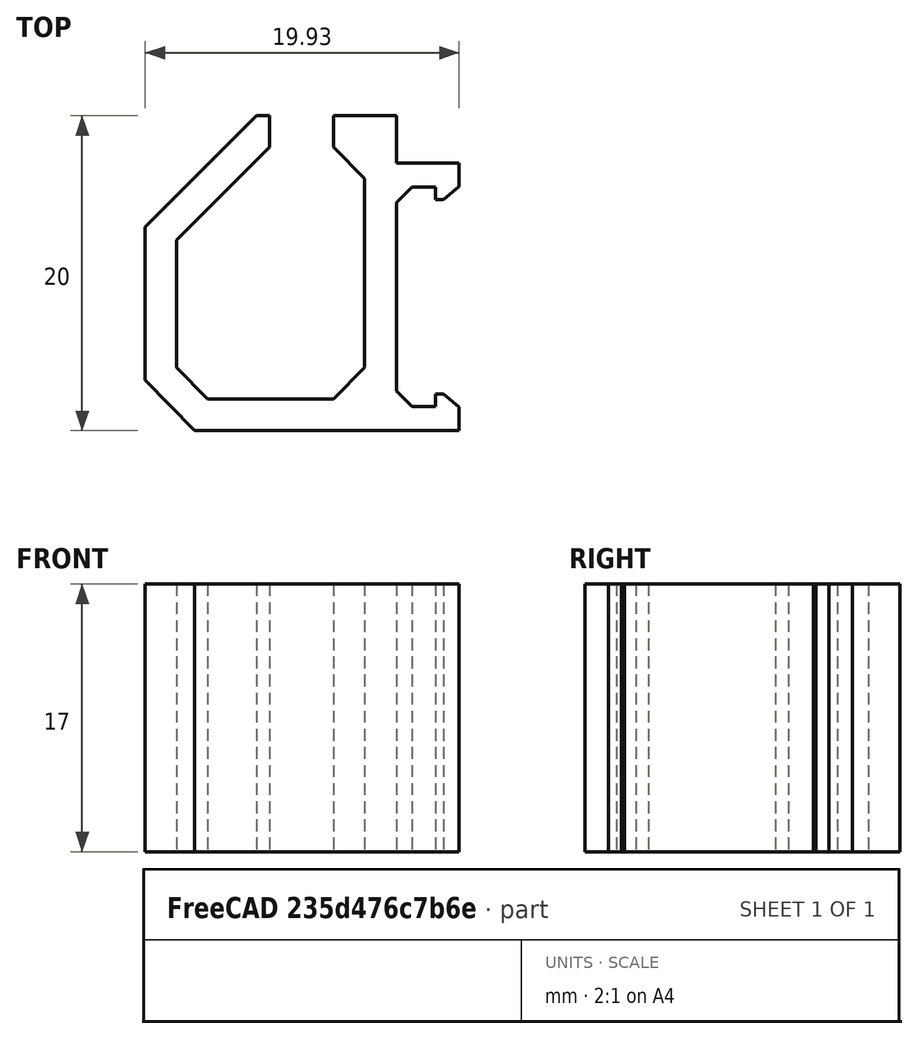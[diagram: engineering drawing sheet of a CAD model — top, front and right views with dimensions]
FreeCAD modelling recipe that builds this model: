
FCSTD DOCUMENT  (FreeCAD 1.1R)
Label: Clip
License: All rights reserved
LicenseURL: https://en.wikipedia.org/wiki/All_rights_reserved
objects: App::Point×1, Sketcher::SketchObject×1, PartDesign::Pad×1, PartDesign::Body×1
note: 6 computed .brp shape members not serialized (recipe doc carries the construction recipe); baked Part::Feature solids carry a one-line shape summary decoded from their .brp

FEATURE [App::Point] Origin001
  Role = Origin
FEATURE [Sketcher::SketchObject] Sketch
  ArcFitTolerance = 1e-06
  AttachmentSupport = -> [Origin]
  ExternalTypes = [0]
  FullyConstrained = false
  MakeInternals = false
  MapMode = 5
  sketch-geometry (38):
    g0: LineSegment StartX=6 StartY=1.52 StartZ=0 EndX=6 EndY=2.32 EndZ=0
    g1: LineSegment StartX=6 StartY=2.32 StartZ=0 EndX=6.5 EndY=2.32 EndZ=0
    g2: LineSegment StartX=6.5 StartY=2.32 StartZ=0 EndX=7.5 EndY=1.5 EndZ=0
    g3: LineSegment StartX=7.5 StartY=1.5 StartZ=0 EndX=7.5 EndY=0 EndZ=0
    g4: LineSegment StartX=7.5 StartY=0 StartZ=0 EndX=-9.3 EndY=0 EndZ=0
    g5: LineSegment StartX=6 StartY=14.68 StartZ=0 EndX=6.5 EndY=14.68 EndZ=0
    g6: LineSegment StartX=6.5 StartY=14.68 StartZ=0 EndX=7.5 EndY=15.5 EndZ=0
    g7: LineSegment StartX=7.5 StartY=15.5 StartZ=0 EndX=7.5 EndY=17 EndZ=0
    g8: LineSegment StartX=7.5 StartY=17 StartZ=0 EndX=3.52 EndY=17 EndZ=0
    g9: LineSegment StartX=6 StartY=14.68 StartZ=0 EndX=6 EndY=15.48 EndZ=0
    g10: LineSegment StartX=6 StartY=15.48 StartZ=0 EndX=4.5 EndY=15.48 EndZ=0
    g11: LineSegment StartX=4.5 StartY=15.48 StartZ=0 EndX=3.52 EndY=14.5 EndZ=0
    g12: LineSegment StartX=3.52 StartY=14.5 StartZ=0 EndX=3.52 EndY=2.5 EndZ=0
    g13: LineSegment StartX=3.52 StartY=2.5 StartZ=0 EndX=4.5 EndY=1.52 EndZ=0
    g14: LineSegment StartX=4.5 StartY=1.52 StartZ=0 EndX=6 EndY=1.52 EndZ=0
    g15: LineSegment [constr] StartX=-32.1952 StartY=8.5 StartZ=0 EndX=30.1278 EndY=8.5 EndZ=0
    g16: LineSegment [constr] StartX=-19.6962 StartY=8.5 StartZ=0 EndX=-19.6962 EndY=0 EndZ=0
    g17: LineSegment [constr] StartX=-19.6962 StartY=8.5 StartZ=0 EndX=-19.6962 EndY=17 EndZ=0
    g18: LineSegment [constr] StartX=-19.6962 StartY=17 StartZ=0 EndX=3.52 EndY=17 EndZ=0
    g19: LineSegment StartX=-9.3 StartY=0 StartZ=0 EndX=-12.4343 EndY=3.22893 EndZ=0
    g20: LineSegment StartX=-12.4343 StartY=3.22893 StartZ=0 EndX=-12.4343 EndY=12.9289 EndZ=0
    g21: LineSegment StartX=-12.4343 StartY=12.9289 StartZ=0 EndX=-5.36326 EndY=20 EndZ=0
    g22: LineSegment StartX=-5.36326 StartY=20 StartZ=0 EndX=-4.53483 EndY=20 EndZ=0
    g23: LineSegment StartX=-4.53483 StartY=20 StartZ=0 EndX=-4.53483 EndY=18 EndZ=0
    g24: LineSegment StartX=-4.53483 StartY=18 StartZ=0 EndX=-10.4343 EndY=12.1005 EndZ=0
    g25: LineSegment StartX=-10.4343 StartY=12.1005 StartZ=0 EndX=-10.4343 EndY=4.02154 EndZ=0
    g26: LineSegment StartX=-10.4343 StartY=4.02154 StartZ=0 EndX=-8.47202 EndY=2 EndZ=0
    g27: LineSegment StartX=-8.47202 StartY=2 StartZ=0 EndX=-0.48 EndY=2 EndZ=0
    g28: LineSegment StartX=-0.48 StartY=2 StartZ=0 EndX=1.5 EndY=4.02154 EndZ=0
    g29: LineSegment StartX=1.5 StartY=4.02154 StartZ=0 EndX=1.5 EndY=16.02 EndZ=0
    g30: LineSegment StartX=1.5 StartY=16.02 StartZ=0 EndX=-0.48 EndY=18 EndZ=0
    g31: LineSegment StartX=-0.48 StartY=18 StartZ=0 EndX=-0.48 EndY=20 EndZ=0
    g32: LineSegment StartX=-0.48 StartY=20 StartZ=0 EndX=3.52 EndY=20 EndZ=0
    g33: LineSegment StartX=3.52 StartY=20 StartZ=0 EndX=3.52 EndY=17 EndZ=0
    g34: LineSegment [constr] StartX=-12.4343 StartY=9.59286 StartZ=0 EndX=-10.4343 EndY=9.59286 EndZ=0
    g35: LineSegment [constr] StartX=-10.5597 StartY=14.8036 StartZ=0 EndX=-9.14546 EndY=13.3894 EndZ=0
    g36: LineSegment [constr] StartX=-5.35806 StartY=2 StartZ=0 EndX=-5.35806 EndY=0 EndZ=0
    g37: LineSegment [constr] StartX=-9.599 StartY=3.161 StartZ=0 EndX=-10.8672 EndY=1.61447 EndZ=0
  constraints (109):
    c: Vertical(g0)
    c: Coincident(g0,g1)
    c: Coincident(g1,g2)
    c: Coincident(g2,g3)
    c: PointOnObject(g3,g-1)
    c: Vertical(g3)
    c: Coincident(g3,g4)
    c: PointOnObject(g4,g-1)
    c: Coincident(g5,g6)
    c: Coincident(g6,g7)
    c: Coincident(g7,g8)
    c: Horizontal(g8)
    c: Coincident(g9,g5)
    c: Vertical(g9)
    c: Coincident(g9,g10)
    c: Parallel(g10,g5)
    c: Coincident(g10,g11)
    c: Coincident(g11,g12)
    c: Vertical(g12)
    c: Coincident(g12,g13)
    c: Coincident(g13,g14)
    c: Coincident(g14,g0)
    c: Horizontal(g14)
    c: Parallel(g10,g14)
    c: Equal(g1,g5)
    c: Horizontal(g1)
    c: PointOnObject(g16,g15)
    c: PointOnObject(g16,g-1)
    c: Vertical(g16)
    c: Coincident(g17,g16)
    c: Coincident(g17,g18)
    c: Coincident(g18,g8)
    c: Horizontal(g18)
    c: Parallel(g17,g16)
    c: Equal(g16,g17)
    c: DistanceY(g-1,g17) = 17
    c: DistanceX(g15,g15) = 62.323
    c: Symmetric(g11,g12,g15)
    c: Symmetric(g10,g13,g15)
    c: Symmetric(g5,g0,g15)
    c: Symmetric(g2,g6,g15)
    c: Perpendicular(g7,g8)
    c: DistanceX(g-1,g3) = 7.5
    c: DistanceY(g7,g7) = 1.5
    c: DistanceX(g5,g6) = 1
    c: DistanceX(g5,g5) = 0.5
    c: DistanceX(g10,g9) = 1.5
    c: Distance(g8,g10) = 1.52
    c: DistanceY(g9,g9) = 0.8
    c: DistanceY(g12,g12) = 12
    c: Angle(g12,g11) = 2.35619
    c: Coincident(g19,g4)
    c: Coincident(g19,g20)
    c: Vertical(g20)
    c: Coincident(g20,g21)
    c: Parallel(g21,g11)
    c: Coincident(g21,g22)
    c: Coincident(g22,g23)
    c: Coincident(g23,g24)
    c: Parallel(g24,g21)
    c: Coincident(g24,g25)
    c: Vertical(g25)
    c: Coincident(g25,g26)
    c: Coincident(g26,g27)
    c: Horizontal(g27)
    c: Coincident(g27,g28)
    c: Coincident(g28,g29)
    c: Vertical(g29)
    c: Coincident(g29,g30)
    c: Perpendicular(g30,g21)
    c: Coincident(g30,g31)
    c: Vertical(g31)
    c: Coincident(g31,g32)
    c: Horizontal(g32)
    c: Coincident(g32,g33)
    c: Coincident(g33,g8)
    c: Perpendicular(g33,g32)
    c: Vertical(g11,g8)
    c: DistanceX(g32,g32) = 4
    c: Distance(g31,g31) = 2
    c: DistanceY(g33,g33) = 3
    c: Equal(g23,g31)
    c: Parallel(g23,g31)
    c: DistanceX(g4,g4) = 16.8
    c: Distance(g25,g20) = 2
    c: PointOnObject(g34,g20)
    c: PointOnObject(g34,g25)
    c: Horizontal(g34)
    c: PointOnObject(g35,g21)
    c: PointOnObject(g35,g24)
    c: Perpendicular(g35,g24)
    c: Equal(g35,g34)
    c: Parallel(g26,g19)
    c: Perpendicular(g22,g23)
    c: Distance(g29,g-2) = 1.5
    c: Vertical(g27,g30)
    c: PointOnObject(g36,g27)
    c: PointOnObject(g36,g4)
    c: Perpendicular(g4,g36)
    c: Equal(g36,g34)
    c: Horizontal(g23,g30)
    c: PointOnObject(g37,g26)
    c: Symmetric(g19,g19,g37)
    c: Perpendicular(g37,g2)
    c: Equal(g37,g34)
    c: Distance(g19,g19) = 4.5
    c: DistanceY(g20,g20) = 9.7
    c: Distance(g21,g21) = 10
    c: Horizontal(g28,g25)
FEATURE [PartDesign::Pad] Pad
  Direction = (0,0,1)
  Length = 17
  Length2 = 10
  Profile = -> Sketch
  ReferenceAxis = -> Sketch [N_Axis]
  Refine = true
  Reversed = true
  SideType = 0
  Suppressed = false
  Type = 0
  Type2 = 0
FEATURE [PartDesign::Body] Body  label="Clip"
  AllowCompound = false
  Group = -> [Sketch,Pad]
  Origin = -> Origin
  Tip = -> Pad
